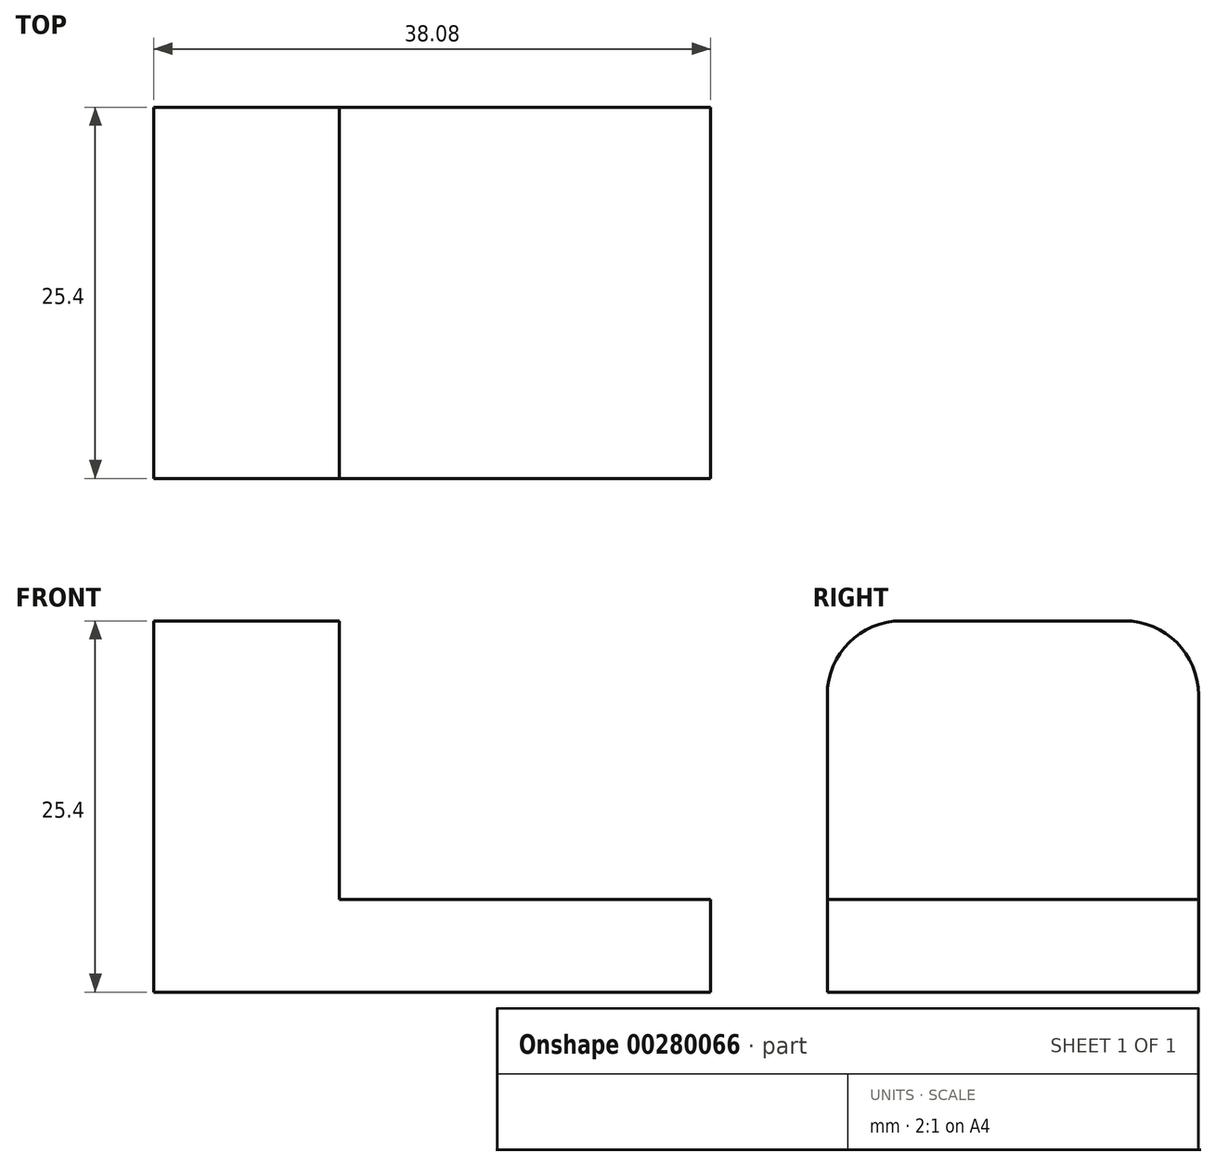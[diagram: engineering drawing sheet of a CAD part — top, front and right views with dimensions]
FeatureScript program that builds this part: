
annotation { "Feature Type Name" : "Feature", "Feature Type Description" : "" }
export const myFeature = defineFeature(function(context is Context, id is Id, definition is map)
    precondition{}
    {
        {
            var Q0;
            Q0=qCreatedBy(makeId("Top.planeOp"),FACE);
            var sketch = newSketch(context, id + "F0", { "sketchPlane" : qUnion([Q0])});
            skLineSegment(sketch, "E0.bottom", {"start": v(0, 0) * mm, "end": v(12.7, 0) * mm});
            skLineSegment(sketch, "E0.top", {"start": v(0, 25.4) * mm, "end": v(12.7, 25.4) * mm});
            skLineSegment(sketch, "E0.left", {"start": v(0, 0) * mm, "end": v(0, 25.4) * mm});
            skLineSegment(sketch, "E0.right", {"start": v(12.7, 0) * mm, "end": v(12.7, 25.4) * mm});
            skSolve(sketch);
        }
        {
            var Q0;
            Q0=qCreatedBy(makeId("Top.planeOp"),FACE);
            var sketch = newSketch(context, id + "F1", { "sketchPlane" : qUnion([Q0])});
            skLineSegment(sketch, "E1.bottom", {"start": v(12.68, 0) * mm, "end": v(38.08, 0) * mm});
            skLineSegment(sketch, "E1.top", {"start": v(12.68, 25.4) * mm, "end": v(38.08, 25.4) * mm});
            skLineSegment(sketch, "E1.left", {"start": v(12.68, 0) * mm, "end": v(12.68, 25.4) * mm});
            skLineSegment(sketch, "E1.right", {"start": v(38.08, 0) * mm, "end": v(38.08, 25.4) * mm});
            skSolve(sketch);
        }
        {
            var Q0;
            Q0 = qSketchRegion(id + "F0", true);
            extrude(context, id + "F2", {"entities" : qUnion([Q0]), "depth" : 25.4 * mm});
        }
        {
            var Q0;
            Q0 = qSketchRegion(id + "F1", true);
            extrude(context, id + "F3", {"entities" : qUnion([Q0]), "operationType" : NewBodyOperationType.ADD, "depth" : 6.35 * mm});
        }
        {
            var Q0;
            Q0=makeQuery(id+"F2.opExtrude","CAP_EDGE",EDGE,{"disambiguationData":[OSD([sQuery(id+"F0.wireOp",EDGE,"E0.bottom")])],"isStart":false});
            var Q1;
            Q1=makeQuery(id+"F2.opExtrude","CAP_EDGE",EDGE,{"disambiguationData":[OSD([sQuery(id+"F0.wireOp",EDGE,"E0.top")])],"isStart":false});
            fillet(context, id + "F4", {"entities" : qUnion([Q0, Q1]), "radius" : 5.08 * mm, "tangentPropagation" : true, "allowEdgeOverflow" : false});
        }
    });
